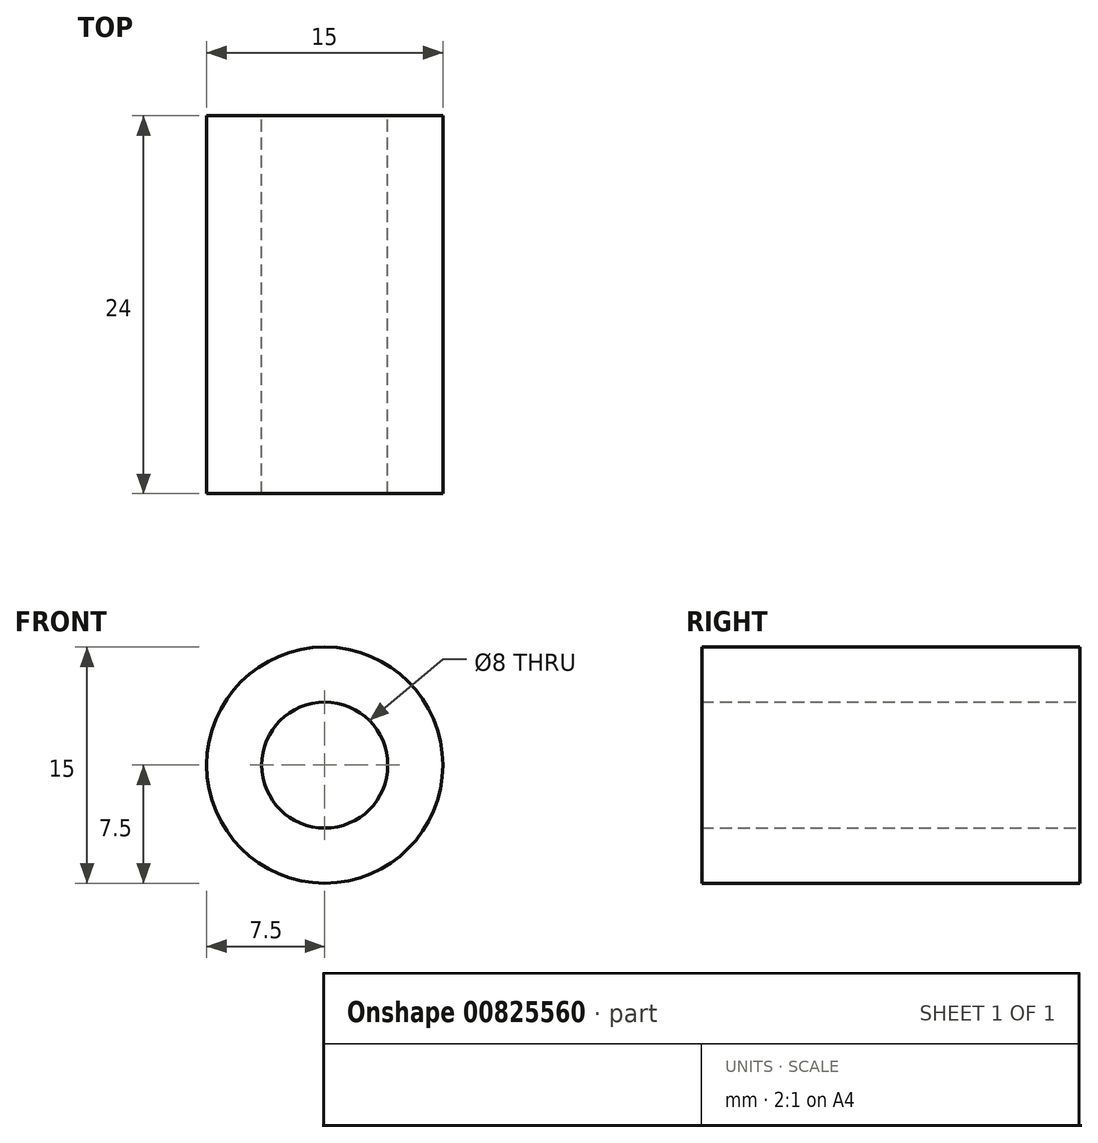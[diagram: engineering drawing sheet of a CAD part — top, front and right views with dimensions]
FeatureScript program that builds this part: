
annotation { "Feature Type Name" : "Feature", "Feature Type Description" : "" }
export const myFeature = defineFeature(function(context is Context, id is Id, definition is map)
    precondition{}
    {
        {
            var Q0;
            Q0=qCreatedBy(makeId("Front.planeOp"),FACE);
            var sketch = newSketch(context, id + "F0", { "sketchPlane" : qUnion([Q0])});
            skCircle(sketch, "E0", {"center": v(0, 0) * mm, "radius": 4 * mm});
            skCircle(sketch, "E1", {"center": v(0, 0) * mm, "radius": 7.5 * mm});
            skSolve(sketch);
        }
        {
            var Q0;
            Q0 = qSketchRegion(id + "F0", true);
            extrude(context, id + "F1", {"entities" : qUnion([Q0]), "depth" : 24 * mm, "offsetDistance" : 25 * mm});
        }
    });
